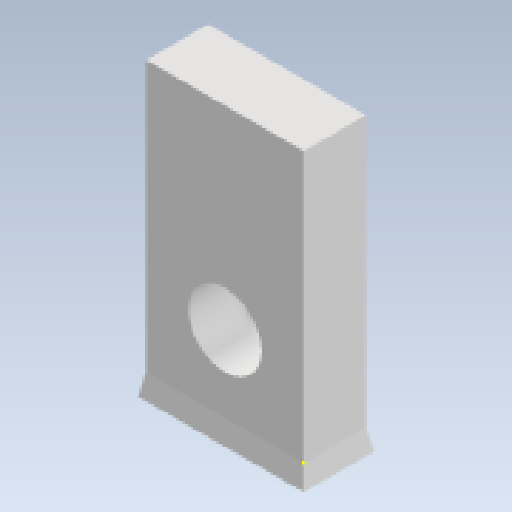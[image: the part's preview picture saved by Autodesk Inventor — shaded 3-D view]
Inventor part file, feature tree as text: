
AUTODESK INVENTOR PART (.ipt)
format: ipt  version: 2023 (Build 270158000, 158)  size: 118,272 bytes
history: native  units: in
note: dims shown in document units (in); Inventor stores cm internally (conversion verified against a paired STEP export)
features: sketch x3, extrude x1, hole x1, fillet x1
ambient origin geometry x8: Origin, YZ Plane, XZ Plane, XY Plane, X Axis, Y Axis, Z Axis, Center Point
bodies: Solid1 (feature_tree)
feature tree (6):
  sketch  "Sketch1"  dims[d0=0.5748in d1=0.2264in]
  extrude  "Extrusion1"  Depth=0.2264in
  hole  "Hole1"  [1 undecoded]
  fillet  "Fillet1"  Radius=0.0787in
  sketch  "Sketch2"  dims[d2=0.5906in d3=0.0787in d4=0.0in d5=0.0687in d6=0.2756in]
  sketch  "Sketch3"  dims[d7=0.266in d8=0.2362in d9=0.507in d10=0.0787in d11=0.5635in d12=0.5in d13=0.8108in d14=0.0787in]
note: 1 required parameter value undecoded (feature->parameter linkage not recoverable at this tier; creation-order binding heuristic only, values carry confidence <= 0.55)
